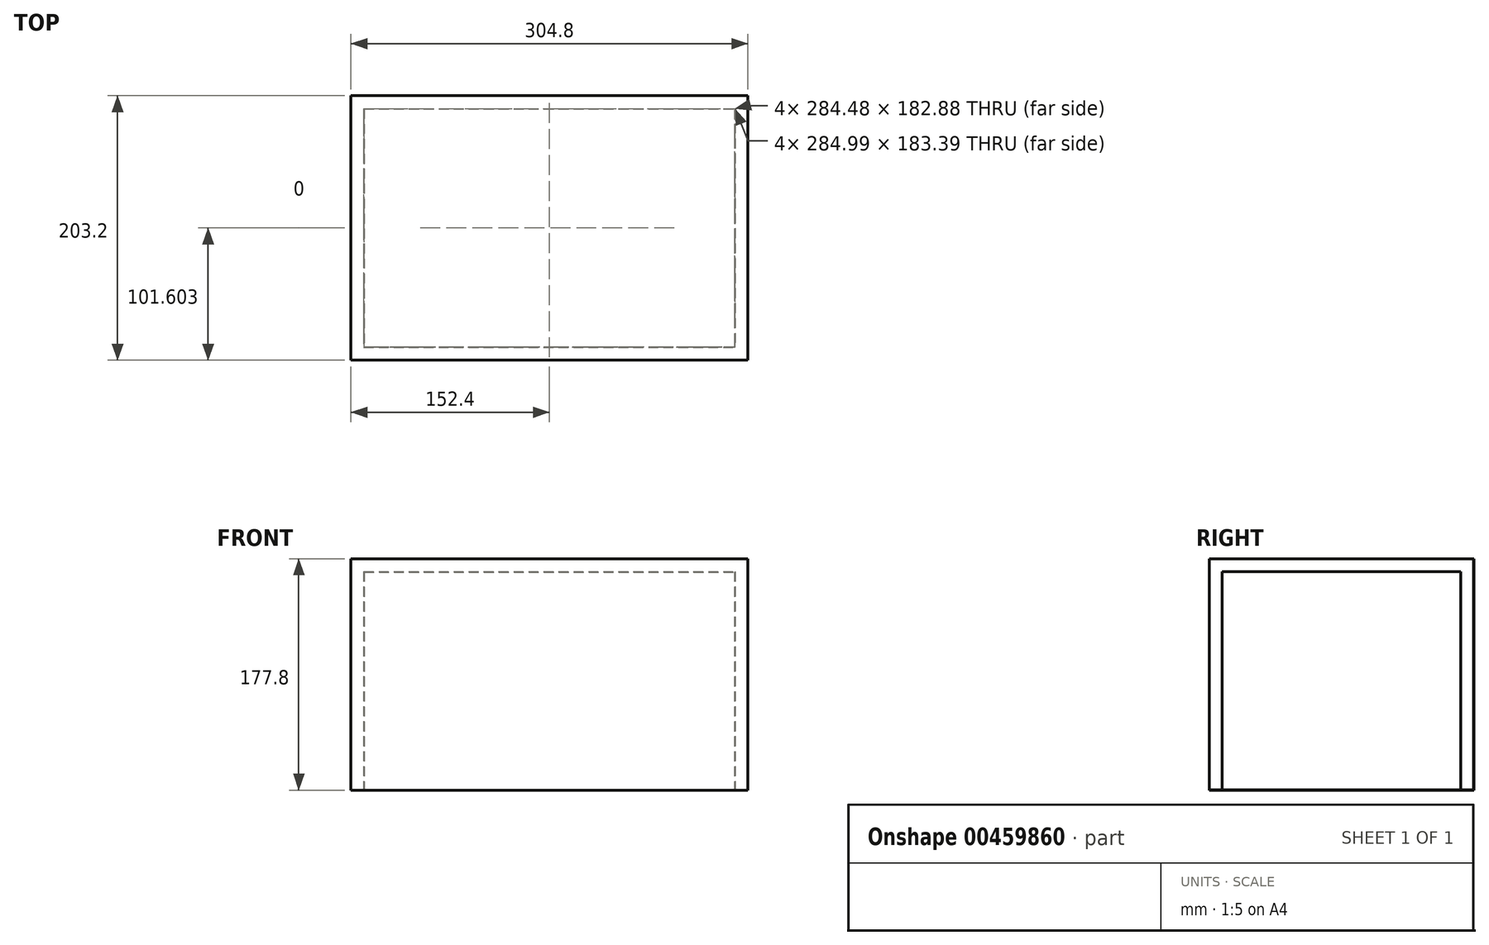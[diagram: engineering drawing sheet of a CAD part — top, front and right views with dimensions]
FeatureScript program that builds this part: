
annotation { "Feature Type Name" : "Feature", "Feature Type Description" : "" }
export const myFeature = defineFeature(function(context is Context, id is Id, definition is map)
    precondition{}
    {
        {
            var Q0;
            Q0=qCreatedBy(makeId("Top.planeOp"),FACE);
            var sketch = newSketch(context, id + "F0", { "sketchPlane" : qUnion([Q0])});
            skLineSegment(sketch, "E0.bottom", {"start": v(-200.9, 76.16) * mm, "end": v(103.9, 76.16) * mm});
            skLineSegment(sketch, "E0.top", {"start": v(-200.9, -127.04) * mm, "end": v(103.9, -127.04) * mm});
            skLineSegment(sketch, "E0.left", {"start": v(-200.9, 76.16) * mm, "end": v(-200.9, -127.04) * mm});
            skLineSegment(sketch, "E0.right", {"start": v(103.9, 76.16) * mm, "end": v(103.9, -127.04) * mm});
            skSolve(sketch);
        }
        {
            var Q0;
            Q0 = qSketchRegion(id + "F0", true);
            extrude(context, id + "F1", {"entities" : qUnion([Q0]), "depth" : 177.8 * mm});
        }
        {
            var Q0;
            Q0=makeQuery(id+"F1.opExtrude","CAP_FACE",FACE,{"disambiguationData":[OSD([sQuery(id+"F0.wireOp",EDGE,"E0.bottom"),sQuery(id+"F0.wireOp",EDGE,"E0.top"),sQuery(id+"F0.wireOp",EDGE,"E0.left"),sQuery(id+"F0.wireOp",EDGE,"E0.right")])],"isStart":true});
            shell(context, id + "F2", {"entities" : qUnion([Q0]), "thickness" : 10.16 * mm});
        }
        {
            var Q0;
            Q0=makeQuery(id+"F1.opExtrude","SWEPT_FACE",FACE,{"disambiguationData":[OSD([sQuery(id+"F0.wireOp",EDGE,"E0.right")])]});
            shell(context, id + "F3", {"entities" : qUnion([Q0]), "thickness" : 0.25 * mm});
        }
    });
